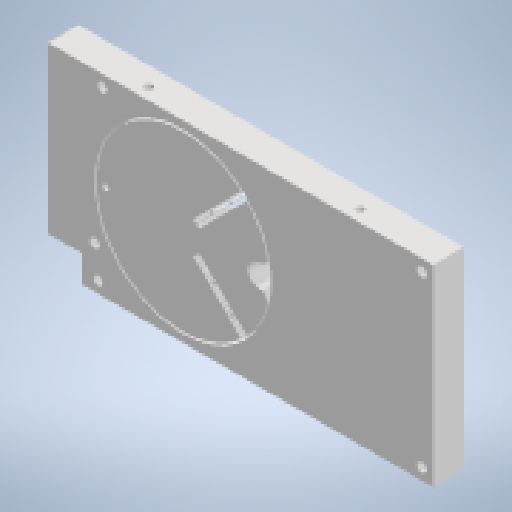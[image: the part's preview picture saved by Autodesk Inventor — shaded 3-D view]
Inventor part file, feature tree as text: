
AUTODESK INVENTOR PART (.ipt)
format: ipt  version: 2023 (Build 270158000, 158)  size: 307,712 bytes
history: native  units: mm
features: extrude x7, sketch x7, other x6, reference x6, fillet x1
ambient origin geometry x8: Origin, YZ Plane, XZ Plane, XY Plane, X Axis, Y Axis, Z Axis, Center Point
bodies: Solid1 (feature_tree)
feature tree (27):
  other  "<userpath>\ClawdDrive\Objet3D\IminaProbe\V3Roue\Settings.xlsx"
  extrude  "Extrusion1"  Depth=100.0mm
  extrude  "Extrusion4"  Depth=5.0mm
  fillet  "Fillet2"  Radius=5.0mm
  extrude  "Extrusion5"  Depth=5.0mm
  extrude  "Extrusion6"  Depth=15.0mm
  extrude  "Extrusion7"  Depth=3.5mm
  extrude  "Extrusion8"  Depth=3.5mm
  extrude  "Extrusion9"  Depth=10.0mm TaperAngle=0.0deg
  sketch  "Sketch1"  dims[d0=50.0mm d1=100.0mm]
  sketch  "Sketch4"  dims[d2=5.0mm d3=5.0mm d4=5.0mm]
  sketch  "Sketch5"  dims[d5=5.0mm d6=5.0mm]
  sketch  "Sketch6"  dims[d7=15.0mm d8=15.0mm]
  reference  "Reference4"
  reference  "Reference5"
  sketch  "Sketch7"  dims[d9=5.0mm d10=3.5mm]
  reference  "Reference6"
  reference  "Reference7"
  reference  "Reference9"
  reference  "Reference10"
  sketch  "Sketch8"  dims[d11=3.5mm d12=3.5mm]
  sketch  "Sketch9"  dims[d13=3.5mm d14=8.0mm d15=0.0mm d22=15.0mm d23=40.0mm d24=20.0mm d25=45.0mm d26=1.6mm d27=6.0mm d28=45.0deg d29=45.0deg d30=46.0mm d31=25.0mm d32=25.0mm d33=25.0mm d34=10.0mm d35=1.0mm d36=1.0mm d37=0.1mm d38=0.05mm d39=0.1mm d40=0.05mm d41=1.0mm d42=1.0mm d43=8.0mm d44=0.0mm d46=2.0mm d47=15.0mm d48=1.5mm d49=9.0mm d50=0.0mm d51=7.0mm d52=1.6mm d53=1.6mm d54=8.0mm d55=0.0mm d56=2.5mm d57=2.5mm d58=2.5mm d59=2.5mm d60=2.5mm d61=8.0mm d62=0.0mm d63=2.5mm d64=3.0mm d65=4.0mm d66=8.0mm d67=0.0mm d68=2.05mm d69=2.05mm d70=2.05mm d71=2.05mm d72=8.0mm d73=0.0mm d74=23.0mm d75=23.0mm d76=55.0mm d77=23.0mm d78=55.0mm d79=5.0mm d80=2.0mm d81=5.0mm d82=2.0mm d83=5.0mm d84=2.0mm d85=5.0mm d86=2.0mm]
  other  "<userpath>\ClawdDrive\Objet3D\IminaProbe\V3Roue\RoueV3.iam"
  other  "RoueV3.iam"
  other  "CapacitiveSensor:1"
  other  "RoueV3PartB:1"
  other  "RoueV3PartC:1"
